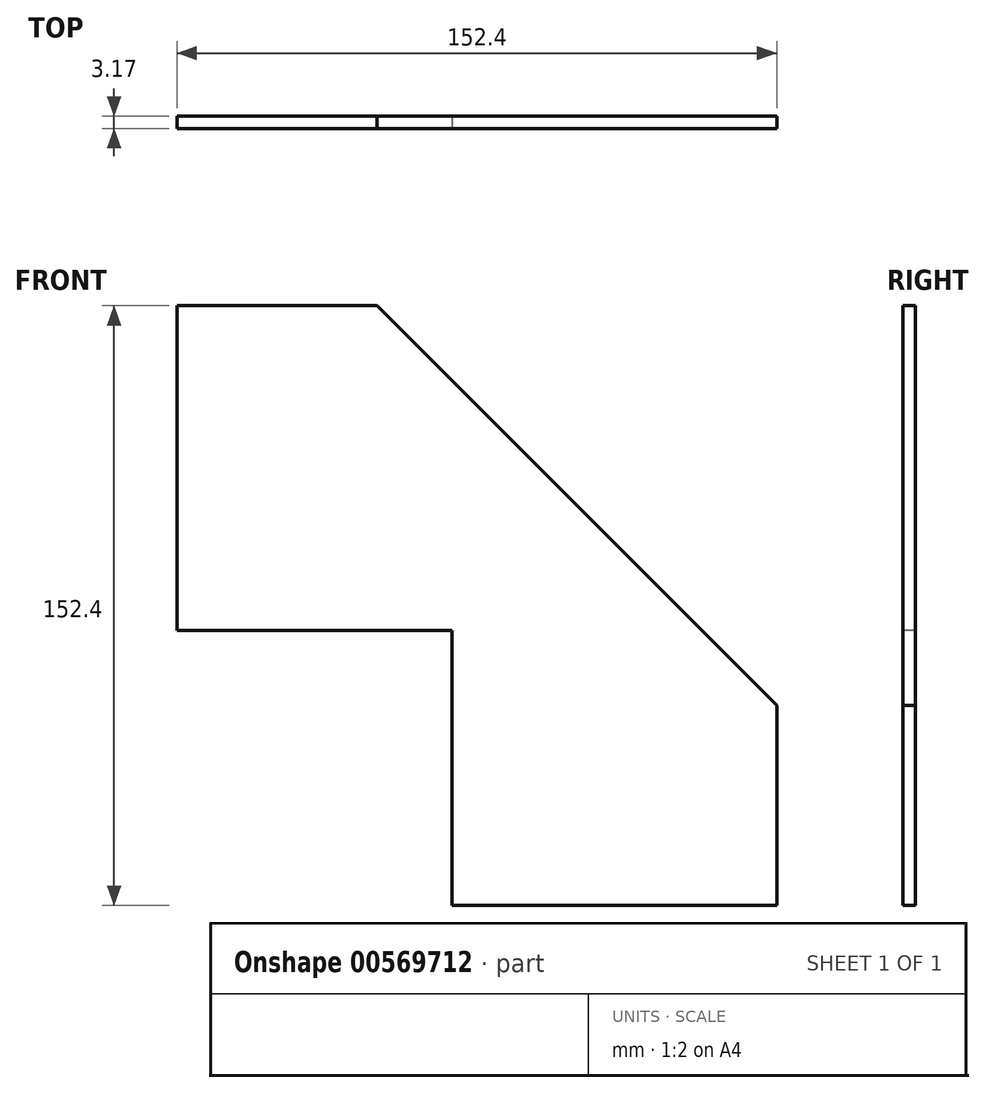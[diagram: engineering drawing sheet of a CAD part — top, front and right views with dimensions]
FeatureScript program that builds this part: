
annotation { "Feature Type Name" : "Feature", "Feature Type Description" : "" }
export const myFeature = defineFeature(function(context is Context, id is Id, definition is map)
    precondition{}
    {
        {
            var Q0;
            Q0=qCreatedBy(makeId("Front.planeOp"),FACE);
            var sketch = newSketch(context, id + "F0", { "sketchPlane" : qUnion([Q0])});
            skLineSegment(sketch, "E0", {"start": v(0, 0) * mm, "end": v(152.4, 0) * mm});
            skLineSegment(sketch, "E1", {"start": v(152.4, 0) * mm, "end": v(152.4, 50.8) * mm});
            skLineSegment(sketch, "E2", {"start": v(152.4, 50.8) * mm, "end": v(50.8, 152.4) * mm});
            skLineSegment(sketch, "E3", {"start": v(50.8, 152.4) * mm, "end": v(0, 152.4) * mm});
            skLineSegment(sketch, "E4", {"start": v(0, 152.4) * mm, "end": v(0, 0) * mm});
            skSolve(sketch);
        }
        {
            var Q0;
            Q0=makeQuery(id+"F0.imprint","IMPRINT",FACE,{"disambiguationData":[TD([[makeQuery(id+"F0.imprint","IMPRINT",EDGE,{"derivedFrom":sQuery(id+"F0.wireOp",EDGE,"E0")}),1.0]])]});
            extrude(context, id + "F1", {"entities" : qUnion([Q0]), "depth" : 3.17 * mm, "offsetDistance" : 25.4 * mm});
        }
        {
            var Q0;
            Q0=makeQuery(id+"F1.opExtrude","CAP_FACE",FACE,{"disambiguationData":[OSD([sQuery(id+"F0.wireOp",EDGE,"E0"),sQuery(id+"F0.wireOp",EDGE,"E1"),sQuery(id+"F0.wireOp",EDGE,"E2"),sQuery(id+"F0.wireOp",EDGE,"E3"),sQuery(id+"F0.wireOp",EDGE,"E4")])],"isStart":false});
            var sketch = newSketch(context, id + "F2", { "sketchPlane" : qUnion([Q0])});
            skLineSegment(sketch, "E5.bottom", {"start": v(0, 0) * mm, "end": v(69.85, 0) * mm});
            skLineSegment(sketch, "E5.top", {"start": v(0, 69.85) * mm, "end": v(69.85, 69.85) * mm});
            skLineSegment(sketch, "E5.left", {"start": v(0, 0) * mm, "end": v(0, 69.85) * mm});
            skLineSegment(sketch, "E5.right", {"start": v(69.85, 0) * mm, "end": v(69.85, 69.85) * mm});
            skSolve(sketch);
        }
        {
            var Q0;
            Q0=makeQuery(id+"F2.imprint","IMPRINT",FACE,{"disambiguationData":[TD([[makeQuery(id+"F2.imprint","IMPRINT",EDGE,{"derivedFrom":sQuery(id+"F2.wireOp",EDGE,"E5.bottom")}),1.0]])]});
            extrude(context, id + "F3", {"entities" : qUnion([Q0]), "operationType" : NewBodyOperationType.REMOVE, "endBound" : BoundingType.UP_TO_NEXT, "oppositeDirection" : true, "depth" : 25.4 * mm, "offsetDistance" : 25.4 * mm});
        }
    });
